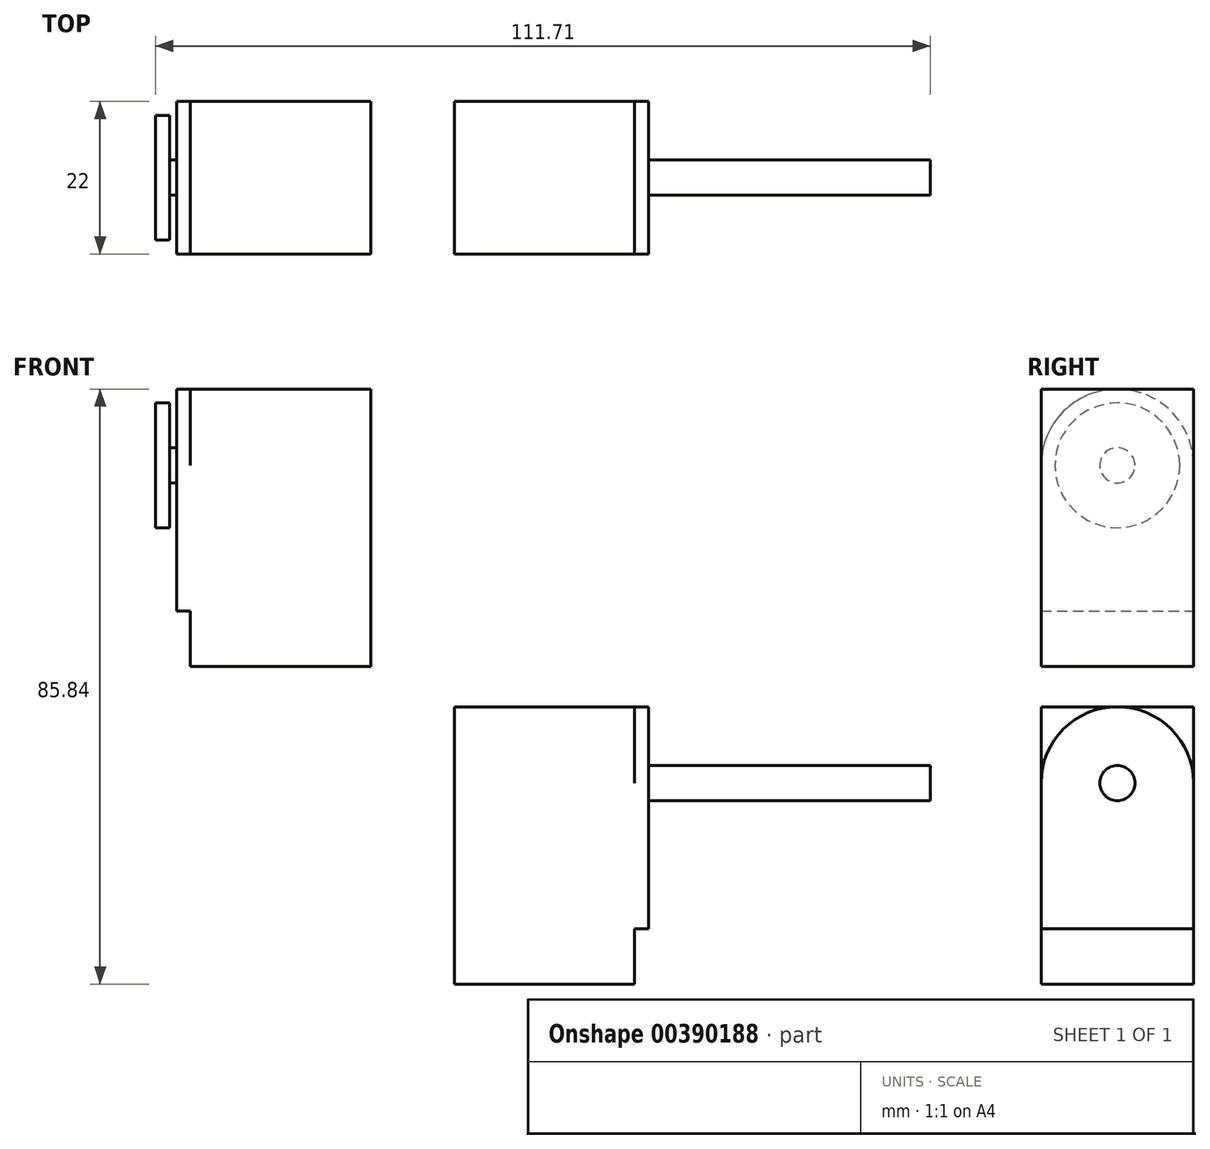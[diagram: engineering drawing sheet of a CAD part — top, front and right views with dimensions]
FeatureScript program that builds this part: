
annotation { "Feature Type Name" : "Feature", "Feature Type Description" : "" }
export const myFeature = defineFeature(function(context is Context, id is Id, definition is map)
    precondition{}
    {
        {
            var Q0;
            Q0=qCreatedBy(makeId("Front.planeOp"),FACE);
            var sketch = newSketch(context, id + "F0", { "sketchPlane" : qUnion([Q0])});
            skLineSegment(sketch, "E0", {"start": v(-15.28, 6.7) * mm, "end": v(10.72, 6.7) * mm});
            skLineSegment(sketch, "E1", {"start": v(10.72, 6.7) * mm, "end": v(10.72, -33.3) * mm});
            skLineSegment(sketch, "E2", {"start": v(10.72, -33.3) * mm, "end": v(-15.28, -33.3) * mm});
            skLineSegment(sketch, "E3", {"start": v(-15.28, -33.3) * mm, "end": v(-15.28, 6.7) * mm});
            skSolve(sketch);
        }
        {
            var Q0;
            Q0=qSketchRegion(id+"F0",true);
            extrude(context, id + "F1", {"entities" : qUnion([Q0]), "depth" : 22 * mm});
        }
        {
            var Q0;
            Q0=makeQuery(id+"F1.opExtrude","SWEPT_FACE",FACE,{"disambiguationData":[OSD([sQuery(id+"F0.wireOp",EDGE,"E1")])]});
            var sketch = newSketch(context, id + "F2", { "sketchPlane" : qUnion([Q0])});
            skLineSegment(sketch, "E4", {"start": v(-22, -25.3) * mm, "end": v(0, -25.3) * mm});
            skLineSegment(sketch, "E5", {"start": v(0, -25.3) * mm, "end": v(0, -4.3) * mm});
            skLineSegment(sketch, "E6", {"start": v(-11, 6.7) * mm, "end": v(-11, 6.7) * mm});
            skLineSegment(sketch, "E7", {"start": v(-22, -4.3) * mm, "end": v(-22, -25.3) * mm});
            skPoint(sketch, "E8.visualSharp", {"position": v(0, 6.7) * mm});
            skArc(sketch, "E8.filletArc", {"start": v(0, -4.3) * mm, "mid": v(-3.22, 3.48) * mm, "end": v(-11, 6.7) * mm});
            skPoint(sketch, "E9.visualSharp", {"position": v(-22, 6.7) * mm});
            skArc(sketch, "E9.filletArc", {"start": v(-11, 6.7) * mm, "mid": v(-18.78, 3.48) * mm, "end": v(-22, -4.3) * mm});
            skSolve(sketch);
        }
        {
            var Q0;
            Q0=makeQuery(id+"F2.imprint","IMPRINT",FACE,{"disambiguationData":[TD([[makeQuery(id+"F2.imprint","IMPRINT",EDGE,{"derivedFrom":sQuery(id+"F2.wireOp",EDGE,"E4")}),1.0]])]});
            extrude(context, id + "F3", {"entities" : qUnion([Q0]), "operationType" : NewBodyOperationType.ADD, "depth" : 2 * mm});
        }
        {
            var Q0;
            Q0=makeQuery(id+"F3.opExtrude","CAP_FACE",FACE,{"disambiguationData":[OSD([sQuery(id+"F2.wireOp",EDGE,"E4"),sQuery(id+"F2.wireOp",EDGE,"E5"),sQuery(id+"F2.wireOp",EDGE,"E7"),sQuery(id+"F2.wireOp",EDGE,"E8.filletArc"),sQuery(id+"F2.wireOp",EDGE,"E9.filletArc")])],"isStart":false});
            var sketch = newSketch(context, id + "F4", { "sketchPlane" : qUnion([Q0])});
            skPoint(sketch, "E10", {"position": v(-11, -4.3) * mm});
            skCircle(sketch, "E11", {"center": v(-11, -4.3) * mm, "radius": 2.54 * mm});
            skSolve(sketch);
        }
        {
            var Q0;
            Q0=makeQuery(id+"F4.imprint","IMPRINT",FACE,{"disambiguationData":[TD([[makeQuery(id+"F4.imprint","IMPRINT",EDGE,{"derivedFrom":sQuery(id+"F4.wireOp",EDGE,"E11")}),1.0]])]});
            extrude(context, id + "F5", {"entities" : qUnion([Q0]), "operationType" : NewBodyOperationType.ADD, "depth" : 40.64 * mm});
        }
        {
            var Q0;
            Q0=qCreatedBy(makeId("Front.planeOp"),FACE);
            var sketch = newSketch(context, id + "F6", { "sketchPlane" : qUnion([Q0])});
            skLineSegment(sketch, "E12", {"start": v(-53.35, 52.54) * mm, "end": v(-27.35, 52.54) * mm});
            skLineSegment(sketch, "E13", {"start": v(-27.35, 52.54) * mm, "end": v(-27.35, 12.54) * mm});
            skLineSegment(sketch, "E14", {"start": v(-27.35, 12.54) * mm, "end": v(-53.35, 12.54) * mm});
            skLineSegment(sketch, "E15", {"start": v(-53.35, 12.54) * mm, "end": v(-53.35, 52.54) * mm});
            skSolve(sketch);
        }
        {
            var Q0;
            Q0=makeQuery(id+"F6.imprint","IMPRINT",FACE,{"disambiguationData":[TD([[makeQuery(id+"F6.imprint","IMPRINT",EDGE,{"derivedFrom":sQuery(id+"F6.wireOp",EDGE,"E12")}),-1.0]])]});
            extrude(context, id + "F7", {"entities" : qUnion([Q0]), "depth" : 22 * mm});
        }
        {
            var Q0;
            Q0=makeQuery(id+"F7.opExtrude","SWEPT_FACE",FACE,{"disambiguationData":[OSD([sQuery(id+"F6.wireOp",EDGE,"E15")])]});
            var sketch = newSketch(context, id + "F8", { "sketchPlane" : qUnion([Q0])});
            skLineSegment(sketch, "E16", {"start": v(0, 20.54) * mm, "end": v(0, 41.54) * mm});
            skLineSegment(sketch, "E17", {"start": v(11, 52.54) * mm, "end": v(11, 52.54) * mm});
            skLineSegment(sketch, "E18", {"start": v(22, 41.54) * mm, "end": v(22, 20.54) * mm});
            skLineSegment(sketch, "E19", {"start": v(22, 20.54) * mm, "end": v(0, 20.54) * mm});
            skPoint(sketch, "E20.visualSharp", {"position": v(0, 52.54) * mm});
            skArc(sketch, "E20.filletArc", {"start": v(11, 52.54) * mm, "mid": v(3.22, 49.32) * mm, "end": v(0, 41.54) * mm});
            skPoint(sketch, "E21.visualSharp", {"position": v(22, 52.54) * mm});
            skArc(sketch, "E21.filletArc", {"start": v(22, 41.54) * mm, "mid": v(18.78, 49.32) * mm, "end": v(11, 52.54) * mm});
            skCircle(sketch, "E22", {"center": v(11, 41.54) * mm, "radius": 2.54 * mm});
            skSolve(sketch);
        }
        {
            var Q0;
            Q0=makeQuery(id+"F8.imprint","IMPRINT",FACE,{"disambiguationData":[TD([[makeQuery(id+"F8.imprint","IMPRINT",EDGE,{"derivedFrom":sQuery(id+"F8.wireOp",EDGE,"E16")}),-1.0]])]});
            var Q1;
            Q1=makeQuery(id+"F8.imprint","IMPRINT",FACE,{"disambiguationData":[TD([[makeQuery(id+"F8.imprint","IMPRINT",EDGE,{"derivedFrom":sQuery(id+"F8.wireOp",EDGE,"E22")}),1.0]])]});
            extrude(context, id + "F9", {"entities" : qUnion([Q0, Q1]), "operationType" : NewBodyOperationType.ADD, "depth" : 2 * mm});
        }
        {
            var Q0;
            Q0=makeQuery(id+"F9.opExtrude","CAP_FACE",FACE,{"disambiguationData":[OSD([sQuery(id+"F8.wireOp",EDGE,"E16"),sQuery(id+"F8.wireOp",EDGE,"E18"),sQuery(id+"F8.wireOp",EDGE,"E19"),sQuery(id+"F8.wireOp",EDGE,"E20.filletArc"),sQuery(id+"F8.wireOp",EDGE,"E21.filletArc")])],"isStart":false});
            var sketch = newSketch(context, id + "F10", { "sketchPlane" : qUnion([Q0])});
            skCircle(sketch, "E23.0", {"center": v(11, 41.54) * mm, "radius": 2.54 * mm});
            skSolve(sketch);
        }
        {
            var Q0;
            Q0=qSketchRegion(id+"F10",true);
            extrude(context, id + "F11", {"entities" : qUnion([Q0]), "operationType" : NewBodyOperationType.ADD, "depth" : 1 * mm});
        }
        {
            var Q0;
            Q0=makeQuery(id+"F11.opExtrude","CAP_FACE",FACE,{"disambiguationData":[OSD([sQuery(id+"F10.wireOp",EDGE,"E23.0")])],"isStart":false});
            var sketch = newSketch(context, id + "F12", { "sketchPlane" : qUnion([Q0])});
            skCircle(sketch, "E24", {"center": v(11, 41.54) * mm, "radius": 9 * mm});
            skSolve(sketch);
        }
        {
            var Q0;
            Q0=makeQuery(id+"F12.imprint","IMPRINT",FACE,{"disambiguationData":[TD([[makeQuery(id+"F12.imprint","IMPRINT",EDGE,{"derivedFrom":makeQuery(id+"F11.opExtrude","CAP_EDGE",EDGE,{"disambiguationData":[OSD([sQuery(id+"F10.wireOp",EDGE,"E23.0")])],"isStart":false})}),1.0]])]});
            var Q1;
            Q1=makeQuery(id+"F12.imprint","IMPRINT",FACE,{"disambiguationData":[TD([[makeQuery(id+"F12.imprint","IMPRINT",EDGE,{"derivedFrom":sQuery(id+"F12.wireOp",EDGE,"E24")}),1.0]])]});
            extrude(context, id + "F13", {"entities" : qUnion([Q0, Q1]), "operationType" : NewBodyOperationType.ADD, "depth" : 2 * mm});
        }
    });
